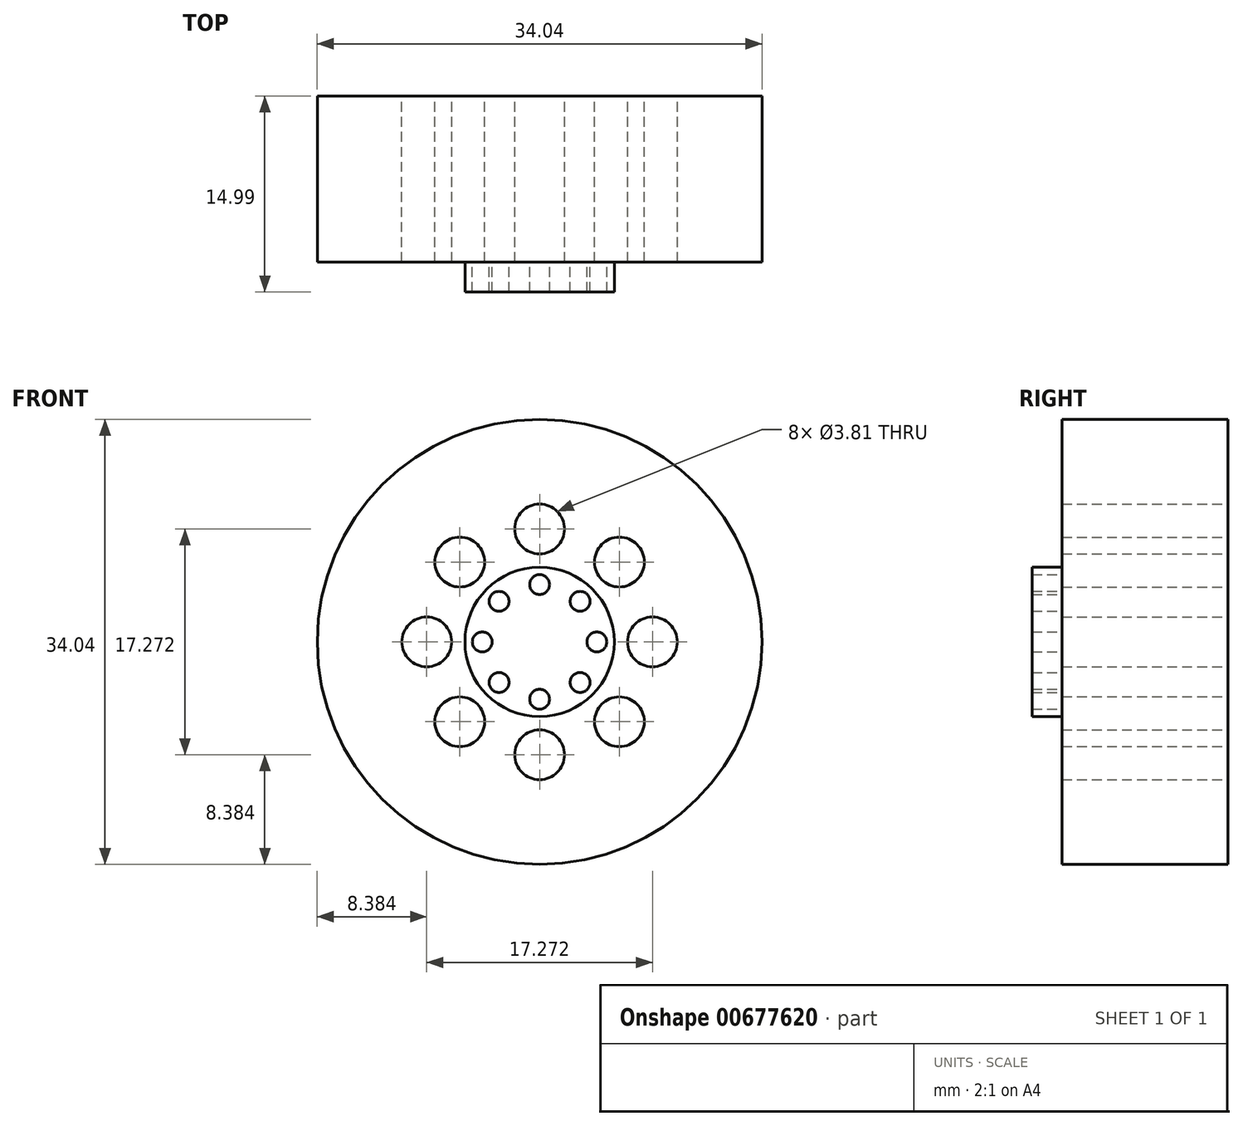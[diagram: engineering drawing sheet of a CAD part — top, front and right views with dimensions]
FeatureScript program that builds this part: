
annotation { "Feature Type Name" : "Feature", "Feature Type Description" : "" }
export const myFeature = defineFeature(function(context is Context, id is Id, definition is map)
    precondition{}
    {
        {
            var Q0;
            Q0=qCreatedBy(makeId("Front.planeOp"),FACE);
            var sketch = newSketch(context, id + "F0", { "sketchPlane" : qUnion([Q0])});
            skCircle(sketch, "E0", {"center": v(0, 0) * mm, "radius": 17.02 * mm});
            skLineSegment(sketch, "E1", {"start": v(0, 0) * mm, "end": v(0, -8.64) * mm});
            skCircle(sketch, "E2", {"center": v(0, -8.64) * mm, "radius": 1.9 * mm});
            skCircle(sketch, "E3.1.0", {"center": v(6.1, -6.1) * mm, "radius": 1.9 * mm});
            skCircle(sketch, "E3.2.0", {"center": v(8.64, 0) * mm, "radius": 1.9 * mm});
            skCircle(sketch, "E3.3.0", {"center": v(6.1, 6.1) * mm, "radius": 1.9 * mm});
            skCircle(sketch, "E3.4.0", {"center": v(0, 8.64) * mm, "radius": 1.9 * mm});
            skCircle(sketch, "E3.5.0", {"center": v(-6.1, 6.1) * mm, "radius": 1.9 * mm});
            skCircle(sketch, "E3.6.0", {"center": v(-8.64, 0) * mm, "radius": 1.9 * mm});
            skCircle(sketch, "E3.7.0", {"center": v(-6.1, -6.1) * mm, "radius": 1.9 * mm});
            skSolve(sketch);
        }
        {
            var Q0;
            Q0 = qSketchRegion(id + "F0", true);
            extrude(context, id + "F1", {"entities" : qUnion([Q0]), "depth" : 12.7 * mm, "offsetDistance" : 25.4 * mm});
        }
        {
            var Q0;
            Q0=makeQuery(id+"F1.opExtrude","CAP_FACE",FACE,{"disambiguationData":[OSD([sQuery(id+"F0.wireOp",EDGE,"E0"),sQuery(id+"F0.wireOp",EDGE,"E2"),sQuery(id+"F0.wireOp",EDGE,"E3.1.0"),sQuery(id+"F0.wireOp",EDGE,"E3.2.0"),sQuery(id+"F0.wireOp",EDGE,"E3.3.0"),sQuery(id+"F0.wireOp",EDGE,"E3.4.0"),sQuery(id+"F0.wireOp",EDGE,"E3.5.0"),sQuery(id+"F0.wireOp",EDGE,"E3.6.0"),sQuery(id+"F0.wireOp",EDGE,"E3.7.0")])],"isStart":false});
            var sketch = newSketch(context, id + "F2", { "sketchPlane" : qUnion([Q0])});
            skCircle(sketch, "E4", {"center": v(0, 0) * mm, "radius": 5.72 * mm});
            skCircle(sketch, "E5", {"center": v(-4.38, 0) * mm, "radius": 0.76 * mm});
            skCircle(sketch, "E6.1.0", {"center": v(-3.1, -3.1) * mm, "radius": 0.76 * mm});
            skCircle(sketch, "E6.2.0", {"center": v(0, -4.38) * mm, "radius": 0.76 * mm});
            skCircle(sketch, "E6.3.0", {"center": v(3.1, -3.1) * mm, "radius": 0.76 * mm});
            skCircle(sketch, "E6.4.0", {"center": v(4.38, 0) * mm, "radius": 0.76 * mm});
            skCircle(sketch, "E6.5.0", {"center": v(3.1, 3.1) * mm, "radius": 0.76 * mm});
            skCircle(sketch, "E6.6.0", {"center": v(0, 4.38) * mm, "radius": 0.76 * mm});
            skCircle(sketch, "E6.7.0", {"center": v(-3.1, 3.1) * mm, "radius": 0.76 * mm});
            skSolve(sketch);
        }
        {
            var Q0;
            Q0 = qSketchRegion(id + "F2", true);
            extrude(context, id + "F3", {"entities" : qUnion([Q0]), "operationType" : NewBodyOperationType.ADD, "depth" : 2.3 * mm, "offsetDistance" : 25.4 * mm});
        }
    });
